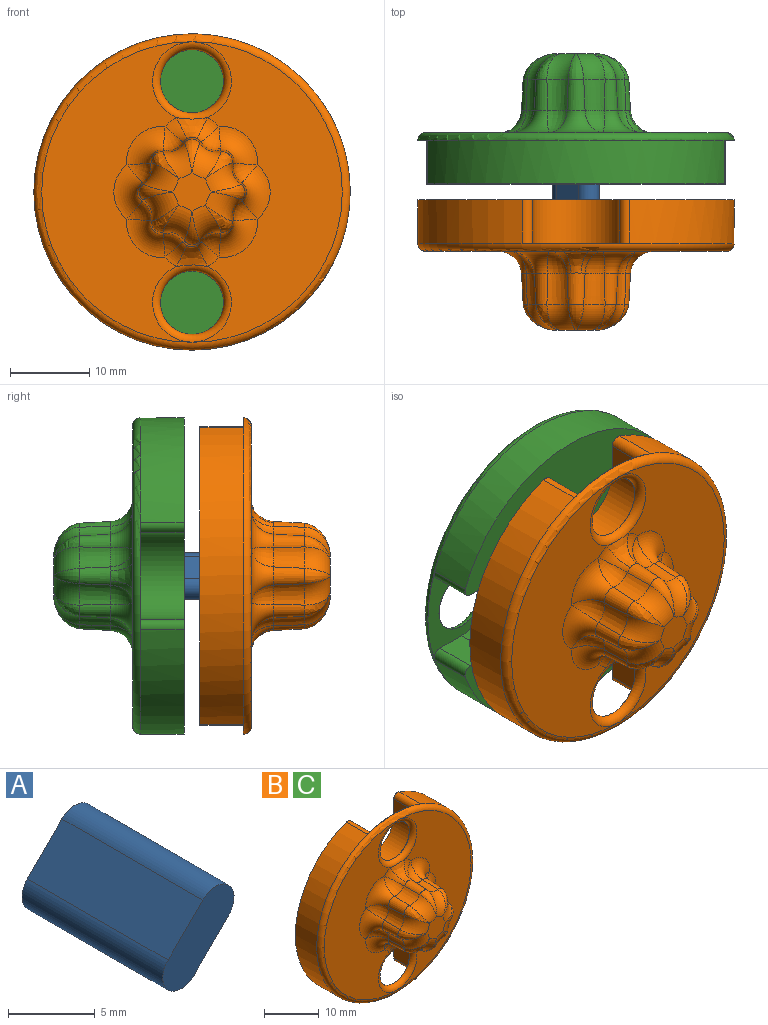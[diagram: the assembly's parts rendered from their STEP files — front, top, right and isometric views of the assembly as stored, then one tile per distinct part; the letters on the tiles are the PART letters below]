
ASSEMBLY  parts=3 mates=2
PART A: 6 faces, bbox 5.8x11.5x5.8 mm
  f0: plane 5.83x5.83mm, normal (0,-1,0), area 19.1mm2, adj f1,f2,f3,f4
  f1: plane 11.5x2.83mm, normal (-0.71,0,0.71), area 46mm2, adj f0,f2,f3,f5
  f2: cylinder r=1.5mm len=11.5mm, axis (0,1,0), area 54.2mm2, adj f0,f1,f4,f5
  f3: cylinder r=1.5mm len=11.5mm, axis (0,1,0), area 54.2mm2, adj f0,f1,f4,f5
  f4: plane 11.5x2.83mm, normal (0.71,0,-0.71), area 46mm2, adj f0,f2,f3,f5
  f5: plane 5.83x5.83mm, normal (0,1,0), area 19.1mm2, adj f1,f2,f3,f4
PART B: 89 faces, bbox 43.3x16.5x43.3 mm
  f0: plane 38.02x38.02mm, normal (0,-1,0), area 695.8mm2, adj f1,f46,f47,f48,f80,f81,f82,f83
  f1: torus R=4.39mm, axis (0,-1,0), area 21.1mm2, adj f0,f2,f44,f45
  f2: bspline ~3.03x2.86mm, area 5.2mm2, adj f1,f3,f46
  f3: cone r=2.36mm half-angle=3deg, axis (0,-1,0), area 11.4mm2, adj f2,f4,f43,f44
  f4: cone r=1.55mm half-angle=3deg, axis (0,1,0), area 9.6mm2, adj f3,f5,f41,f46
  f5: bspline ~3.38x3.37mm, area 4.6mm2, adj f4,f6,f43
  f6: torus R=6.21mm, axis (0,-1,0), area 14mm2, adj f5,f7,f40,f41
  f7: plane 4.83x4.83mm, normal (0,-1,0), area 15.8mm2, adj f6,f8,f34,f35,f36,f37,f39,f43
  f8: torus R=6.21mm, axis (0,-1,0), area 14mm2, adj f7,f9,f17,f18,f33
  f9: bspline ~3.02x2.67mm, area 3.8mm2, adj f8,f10,f39
  f10: cone r=1.55mm half-angle=3deg, axis (0,1,0), area 9.6mm2, adj f9,f11,f16,f18,f84,f86
  f11: cone r=2.36mm half-angle=3deg, axis (0,-1,0), area 11.4mm2, adj f10,f12,f13,f39
  f12: bspline ~3.03x2.86mm, area 5.2mm2, adj f11,f86,f87
  f13: cone r=1.55mm half-angle=3deg, axis (0,1,0), area 9.6mm2, adj f11,f14,f15,f87
  f14: bspline ~3.38x3.37mm, area 4.6mm2, adj f13,f37,f39
  f15: cone r=2.36mm half-angle=3deg, axis (0,-1,0), area 11.4mm2, adj f13,f37,f44,f45
  f16: bspline ~4.88x3.08mm, area 9mm2, adj f10,f84,f85,f86
  f17: bspline ~2.03x0.58mm, area 0.1mm2, adj f8,f39
  f18: cone r=2.36mm half-angle=3deg, axis (0,-1,0), area 11.4mm2, adj f8,f10,f19,f32
  f19: cone r=1.55mm half-angle=3deg, axis (0,1,0), area 9.6mm2, adj f18,f20,f33,f83
  f20: cone r=2.36mm half-angle=3deg, axis (0,-1,0), area 11.4mm2, adj f19,f21,f31,f34
  f21: cone r=1.55mm half-angle=3deg, axis (0,1,0), area 9.6mm2, adj f20,f22,f23,f82
  f22: bspline ~4.27x3.32mm, area 5.2mm2, adj f21,f34,f35
  f23: cone r=2.36mm half-angle=3deg, axis (0,-1,0), area 11.4mm2, adj f21,f24,f30,f35
  f24: cone r=1.55mm half-angle=3deg, axis (0,1,0), area 9.6mm2, adj f23,f25,f26,f81
  f25: bspline ~3.38x3.37mm, area 4.6mm2, adj f24,f35,f36
  f26: cone r=2.36mm half-angle=3deg, axis (0,-1,0), area 11.4mm2, adj f24,f27,f29,f36
  f27: cone r=1.55mm half-angle=3deg, axis (0,1,0), area 9.6mm2, adj f26,f28,f40,f41,f47,f80
  f28: bspline ~4.88x3.08mm, area 9mm2, adj f27,f47,f48,f80
  f29: bspline ~3.03x2.86mm, area 5.2mm2, adj f26,f80,f81
  f30: bspline ~3.03x2.86mm, area 5.2mm2, adj f23,f81,f82
  f31: bspline ~3.03x2.86mm, area 5.2mm2, adj f20,f82,f83
  f32: bspline ~3.03x2.86mm, area 5.2mm2, adj f18,f83,f84
  f33: bspline ~3.38x3.37mm, area 4.6mm2, adj f8,f19,f34
  f34: torus R=6.21mm, axis (0,-1,0), area 14mm2, adj f7,f20,f22,f33
  f35: torus R=6.21mm, axis (0,-1,0), area 14mm2, adj f7,f22,f23,f25
  f36: torus R=6.21mm, axis (0,-1,0), area 14mm2, adj f7,f25,f26,f40
  f37: torus R=6.21mm, axis (0,-1,0), area 14mm2, adj f7,f14,f15,f38
  f38: bspline ~4.27x3.32mm, area 5.5mm2, adj f37,f43,f44
  f39: torus R=6.21mm, axis (0,-1,0), area 14mm2, adj f7,f9,f11,f14,f17
  f40: bspline ~4.27x3.32mm, area 5.4mm2, adj f6,f27,f36
  f41: cone r=2.36mm half-angle=3deg, axis (0,-1,0), area 11.4mm2, adj f4,f6,f27,f42
  f42: bspline ~3.03x2.86mm, area 5.2mm2, adj f41,f46,f47
  f43: torus R=6.21mm, axis (0,-1,0), area 14mm2, adj f3,f5,f7,f38
  f44: cone r=1.55mm half-angle=3deg, axis (0,1,0), area 9.6mm2, adj f1,f3,f15,f38
  f45: bspline ~3.03x2.86mm, area 5.2mm2, adj f1,f15,f87
  f46: torus R=4.39mm, axis (0,-1,0), area 21.1mm2, adj f0,f2,f4,f42
  f47: torus R=4.39mm, axis (0,-1,0), area 5.2mm2, adj f0,f27,f28,f42
  f48: torus R=4.99mm, axis (0,-1,0), area 42.2mm2, adj f0,f28,f49
  f49: cylinder r=4mm len=8mm, axis (0,1,0), area 0.3mm2, adj f48,f50
  f50: plane 13.66x11.5mm, normal (0,1,0), area 61.3mm2, adj f49,f51,f75,f76,f77,f78,f79
  f51: cylinder r=0.99mm len=5.5mm, axis (0,1,0), area 10.5mm2, adj f50,f52,f75,f79
  f52: plane 40x37.72mm, normal (0,1,0), area 856.8mm2, adj f51,f53,f56,f57,f58,f59,f60,f75
  f53: cylinder r=0.99mm len=5.5mm, axis (0,1,0), area 10.5mm2, adj f52,f54,f56,f79
  f54: plane 13.66x11.5mm, normal (0,1,0), area 61.3mm2, adj f53,f55,f56,f57,f58,f59,f79
  f55: cylinder r=4mm len=8mm, axis (0,1,0), area 0.3mm2, adj f54,f85
  f56: plane 5.5x3.87mm, normal (1,0,0), area 21.3mm2, adj f52,f53,f54,f57
  f57: cylinder r=5.5mm len=11mm, axis (0,1,0), area 95mm2, adj f52,f54,f56,f58
  f58: plane 5.5x3.87mm, normal (-1,0,0), area 21.3mm2, adj f52,f54,f57,f59
  f59: cylinder r=0.99mm len=5.5mm, axis (0,1,0), area 10.5mm2, adj f52,f54,f58,f79
  f60: cylinder r=7.5mm len=15mm, axis (0,1,0), area 235.6mm2, adj f52,f61
  f61: torus R=7mm, axis (0,1,0), area 36.1mm2, adj f60,f62
  f62: plane 14x14mm, normal (0,1,0), area 75.4mm2, adj f61,f63
  f63: torus R=5mm, axis (0,1,0), area 23.1mm2, adj f62,f64
  f64: cylinder r=4.5mm len=9mm, axis (0,1,0), area 141.4mm2, adj f63,f65
  f65: plane 9x9mm, normal (0,1,0), area 28.6mm2, adj f64,f66,f72,f73,f74
  f66: torus R=2.3mm, axis (0,-1,0), area 4.9mm2, adj f65,f67,f72,f74
  f67: cylinder r=1.8mm len=5mm, axis (0,1,0), area 28.3mm2, adj f66,f68,f70,f71
  f68: plane 5x2.83mm, normal (0.71,0,-0.71), area 20mm2, adj f67,f69,f71,f74
  f69: cylinder r=1.8mm len=5mm, axis (0,1,0), area 28.3mm2, adj f68,f70,f71,f73
  f70: plane 5x2.83mm, normal (-0.71,0,0.71), area 20mm2, adj f67,f69,f71,f72
  f71: plane 6.43x6.43mm, normal (0,1,0), area 24.6mm2, adj f67,f68,f69,f70
  f72: cylinder r=0.5mm len=3.18mm, axis (-0.71,0,-0.71), area 3.1mm2, adj f65,f66,f70,f73
  f73: torus R=2.3mm, axis (0,-1,0), area 4.9mm2, adj f65,f69,f72,f74
  f74: cylinder r=0.5mm len=3.18mm, axis (0.71,0,0.71), area 3.1mm2, adj f65,f66,f68,f73
  f75: plane 5.5x3.87mm, normal (1,0,0), area 21.3mm2, adj f50,f51,f52,f76
  f76: cylinder r=5.5mm len=11mm, axis (0,1,0), area 95mm2, adj f50,f52,f75,f77
  f77: plane 5.5x3.87mm, normal (-1,0,0), area 21.3mm2, adj f50,f52,f76,f78
  f78: cylinder r=0.99mm len=5.5mm, axis (0,1,0), area 10.5mm2, adj f50,f52,f77,f79
  f79: cylinder r=20mm len=40mm, axis (0,1,0), area 539.1mm2, adj f50,f51,f52,f53,f54,f59,f78,f88
  f80: torus R=4.39mm, axis (0,-1,0), area 5.2mm2, adj f0,f27,f28,f29
  f81: torus R=4.39mm, axis (0,-1,0), area 21.1mm2, adj f0,f24,f29,f30
  f82: torus R=4.39mm, axis (0,-1,0), area 21.1mm2, adj f0,f21,f30,f31
  f83: torus R=4.39mm, axis (0,-1,0), area 21.1mm2, adj f0,f19,f31,f32
  f84: torus R=4.39mm, axis (0,-1,0), area 5.2mm2, adj f0,f10,f16,f32
  f85: torus R=4.99mm, axis (0,-1,0), area 42mm2, adj f0,f16,f55
  f86: torus R=4.39mm, axis (0,-1,0), area 5.2mm2, adj f0,f10,f12,f16
  f87: torus R=4.39mm, axis (0,-1,0), area 21.1mm2, adj f0,f12,f13,f45
  f88: torus R=19.01mm, axis (0,-1,0), area 191.9mm2, adj f0,f79
PART C: same geometry as B
PLACE A rot(axis=(0,-1,0),180deg) t=(14.41,0.52,99.14)mm
PLACE B t=(14.41,1.02,99.14)mm
PLACE C rot(axis=(0.71,0,0.71),180deg) t=(14.41,3.02,99.14)mm
MATE fastened A.f0 <-> B.f60  axis (0,-1,0) through (14.41,-4.48,99.14)mm
MATE slider A.f5 <-> C.f60  axis (0,1,0) through (14.41,7.02,99.14)mm
